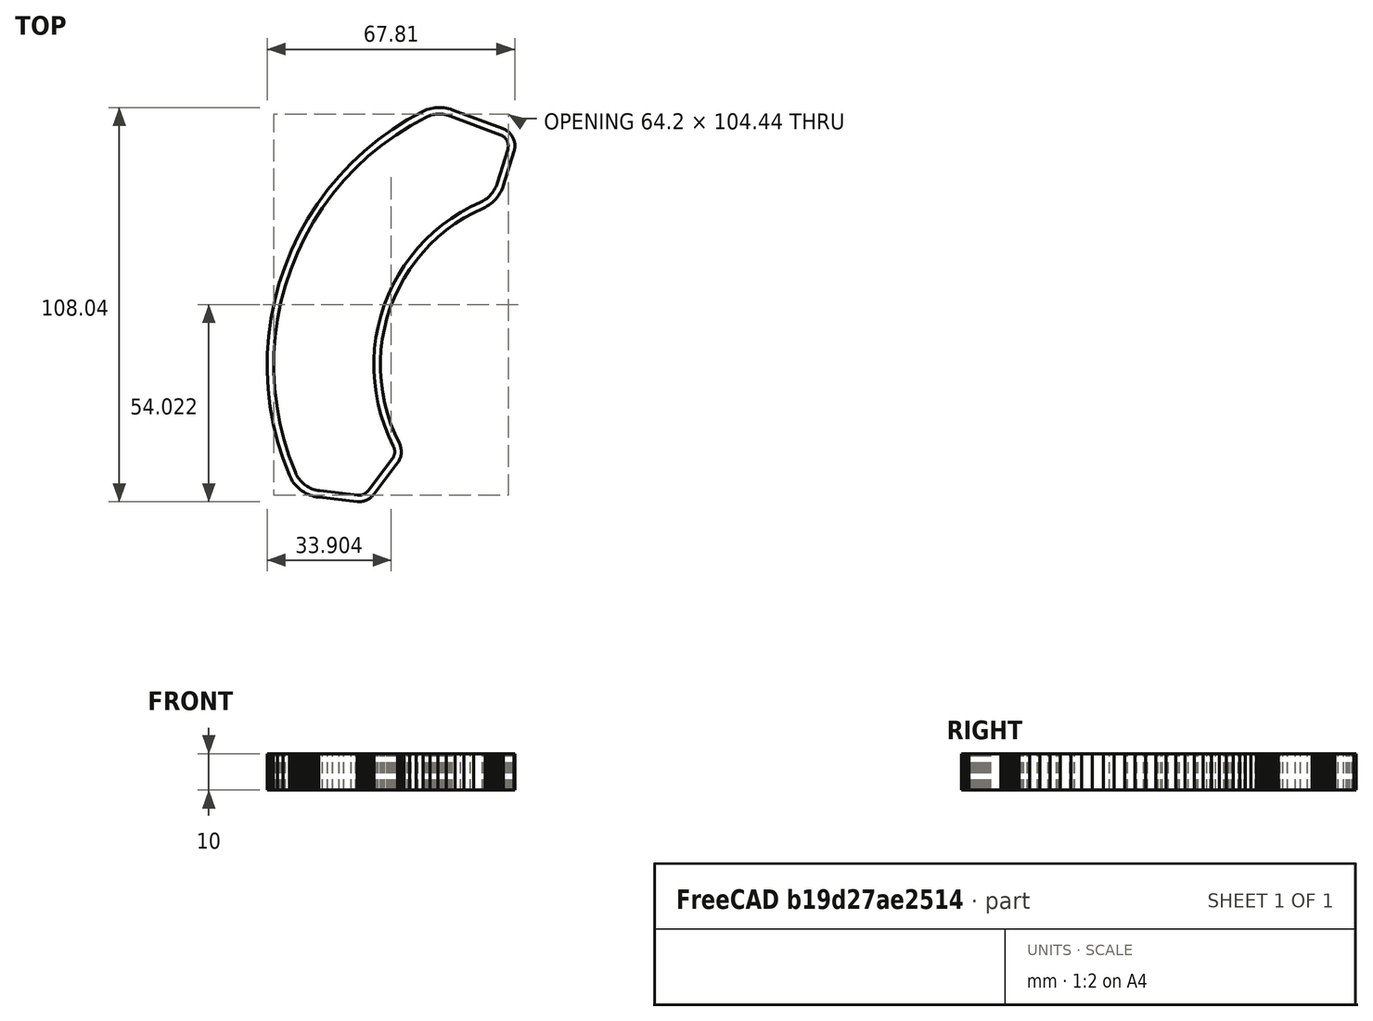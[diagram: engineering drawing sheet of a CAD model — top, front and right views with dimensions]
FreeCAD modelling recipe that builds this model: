
FCSTD DOCUMENT  (FreeCAD 1.0R39109 (Git))
Label: oledprofile
License: All rights reserved
LicenseURL: https://en.wikipedia.org/wiki/All_rights_reserved
objects: Part::Feature×1, Part::Refine×1, Part::Part2DObjectPython×1, Sketcher::SketchObject×1, PartDesign::Pad×1, PartDesign::Body×1
note: 9 computed .brp shape members not serialized (recipe doc carries the construction recipe); baked Part::Feature solids carry a one-line shape summary decoded from their .brp

FEATURE [Part::Feature] oledpart001_solid001  label="oledpart001 (Solid)001"
  shape: bbox 67.8 x 108 x 4 mm, 10964 faces (baked)
FEATURE [Part::Refine] oledpart001_solid002  label="oledpart001 (Solid)002"
  Placement = pos=(-283,298,0) rot=(0,0,1;0rad)
  Source = -> oledpart001_solid001
FEATURE [Part::Part2DObjectPython] Shape2DView  # Draft 2D object (typed FeaturePython)
  AutoUpdate = true
  Base = -> oledpart001_solid002
  Clip = false
  FuseArch = false
  HiddenLines = false
  InPlace = true
  OnlySolids = false
  Projection = (0,0,1)
  ProjectionMode = 0
  SegmentLength = 0.05
  Tessellation = false
  VisibleOnly = false
FEATURE [Sketcher::SketchObject] Sketch
  ArcFitTolerance = 1e-06
  FullyConstrained = false
  MakeInternals = false
  sketch-geometry (2716):
    g0: LineSegment StartX=4.71191 StartY=-20.0049 StartZ=0 EndX=4.70312 EndY=-17.0566 EndZ=0
    g1: LineSegment StartX=4.70312 StartY=-17.0566 StartZ=0 EndX=4.87988 EndY=-14.1143 EndZ=0
    g2: LineSegment StartX=4.87988 StartY=-14.1143 StartZ=0 EndX=5.24121 EndY=-11.1885 EndZ=0
    g3: LineSegment StartX=5.24121 StartY=-11.1885 StartZ=0 EndX=5.78613 EndY=-8.29102 EndZ=0
    g4: LineSegment StartX=5.78613 StartY=-8.29102 StartZ=0 EndX=6.51074 EndY=-5.43262 EndZ=0
    g5: LineSegment StartX=6.51074 StartY=-5.43262 StartZ=0 EndX=7.41406 EndY=-2.62695 EndZ=0
    g6: LineSegment StartX=7.41406 StartY=-2.62695 StartZ=0 EndX=8.49121 EndY=0.118164 EndZ=0
    g7: LineSegment StartX=8.49121 StartY=0.118164 StartZ=0 EndX=9.73828 EndY=2.78906 EndZ=0
    g8: LineSegment StartX=9.73828 StartY=2.78906 StartZ=0 EndX=11.1514 EndY=5.37695 EndZ=0
    g9: LineSegment StartX=11.1514 StartY=5.37695 StartZ=0 EndX=12.7236 EndY=7.87012 EndZ=0
    g10: LineSegment StartX=12.7236 StartY=7.87012 StartZ=0 EndX=14.4492 EndY=10.2607 EndZ=0
    g11: LineSegment StartX=14.4492 StartY=10.2607 StartZ=0 EndX=16.3213 EndY=12.5381 EndZ=0
    g12: LineSegment StartX=16.3213 StartY=12.5381 StartZ=0 EndX=18.332 EndY=14.6934 EndZ=0
    g13: LineSegment StartX=18.332 StartY=14.6934 StartZ=0 EndX=20.4756 EndY=16.7188 EndZ=0
    g14: LineSegment StartX=20.4756 StartY=16.7188 StartZ=0 EndX=22.7412 EndY=18.6045 EndZ=0
    g15: LineSegment StartX=22.7412 StartY=18.6045 StartZ=0 EndX=25.1201 EndY=20.3457 EndZ=0
    g16: LineSegment StartX=25.1201 StartY=20.3457 StartZ=0 EndX=27.6045 EndY=21.9326 EndZ=0
    g17: LineSegment StartX=27.6045 StartY=21.9326 StartZ=0 EndX=30.1836 EndY=23.3613 EndZ=0
    g18: LineSegment StartX=30.1836 StartY=23.3613 StartZ=0 EndX=32.8467 EndY=24.626 EndZ=0
    g19: LineSegment StartX=32.8467 StartY=24.626 StartZ=0 EndX=33.4014 EndY=24.8887 EndZ=0
    g20: LineSegment StartX=33.4014 StartY=24.8887 StartZ=0 EndX=33.9395 EndY=25.1855 EndZ=0
    g21: LineSegment StartX=33.9395 StartY=25.1855 StartZ=0 EndX=34.459 EndY=25.5146 EndZ=0
    g22: LineSegment StartX=34.459 StartY=25.5146 StartZ=0 EndX=34.9561 EndY=25.875 EndZ=0
    g23: LineSegment StartX=34.9561 StartY=25.875 StartZ=0 EndX=35.4307 EndY=26.2646 EndZ=0
    g24: LineSegment StartX=35.4307 StartY=26.2646 StartZ=0 EndX=35.8799 EndY=26.6836 EndZ=0
    g25: LineSegment StartX=35.8799 StartY=26.6836 StartZ=0 EndX=36.3037 EndY=27.1289 EndZ=0
    g26: LineSegment StartX=36.3037 StartY=27.1289 StartZ=0 EndX=36.6982 EndY=27.5996 EndZ=0
    g27: LineSegment StartX=36.6982 StartY=27.5996 StartZ=0 EndX=37.0635 EndY=28.0928 EndZ=0
    g28: LineSegment StartX=37.0635 StartY=28.0928 StartZ=0 EndX=37.3975 EndY=28.6084 EndZ=0
    g29: LineSegment StartX=37.3975 StartY=28.6084 StartZ=0 EndX=37.7002 EndY=29.1436 EndZ=0
    g30: LineSegment StartX=37.7002 StartY=29.1436 StartZ=0 EndX=37.9688 EndY=29.6963 EndZ=0
    g31: LineSegment StartX=37.9688 StartY=29.6963 StartZ=0 EndX=38.2021 EndY=30.2637 EndZ=0
    g32: LineSegment StartX=38.2021 StartY=30.2637 StartZ=0 EndX=38.4014 EndY=30.8447 EndZ=0
    g33: LineSegment StartX=38.4014 StartY=30.8447 StartZ=0 EndX=41.2842 EndY=40.2012 EndZ=0
    g34: LineSegment StartX=41.2842 StartY=40.2012 StartZ=0 EndX=41.3643 EndY=40.4922 EndZ=0
    g35: LineSegment StartX=41.3643 StartY=40.4922 StartZ=0 EndX=41.4268 EndY=40.7881 EndZ=0
    g36: LineSegment StartX=41.4268 StartY=40.7881 StartZ=0 EndX=41.4717 EndY=41.0869 EndZ=0
    g37: LineSegment StartX=41.4717 StartY=41.0869 StartZ=0 EndX=41.498 EndY=41.3877 EndZ=0
    g38: LineSegment StartX=41.498 StartY=41.3877 StartZ=0 EndX=41.5059 EndY=41.6895 EndZ=0
    g39: LineSegment StartX=41.5059 StartY=41.6895 StartZ=0 EndX=41.4961 EndY=41.9912 EndZ=0
    g40: LineSegment StartX=41.4961 StartY=41.9912 StartZ=0 EndX=41.4678 EndY=42.292 EndZ=0
    g41: LineSegment StartX=41.4678 StartY=42.292 StartZ=0 EndX=41.4209 EndY=42.5908 EndZ=0
    g42: LineSegment StartX=41.4209 StartY=42.5908 StartZ=0 EndX=41.3564 EndY=42.8857 EndZ=0
    g43: LineSegment StartX=41.3564 StartY=42.8857 StartZ=0 EndX=41.2744 EndY=43.1768 EndZ=0
    g44: LineSegment StartX=41.2744 StartY=43.1768 StartZ=0 EndX=41.1748 EndY=43.4619 EndZ=0
    g45: LineSegment StartX=41.1748 StartY=43.4619 StartZ=0 EndX=41.0586 EndY=43.7412 EndZ=0
    g46: LineSegment StartX=41.0586 StartY=43.7412 StartZ=0 EndX=40.9258 EndY=44.0127 EndZ=0
    g47: LineSegment StartX=40.9258 StartY=44.0127 StartZ=0 EndX=40.7764 EndY=44.2754 EndZ=0
    g48: LineSegment StartX=40.7764 StartY=44.2754 StartZ=0 EndX=40.6113 EndY=44.5283 EndZ=0
    g49: LineSegment StartX=40.6113 StartY=44.5283 StartZ=0 EndX=40.4307 EndY=44.7705 EndZ=0
    g50: LineSegment StartX=40.4307 StartY=44.7705 StartZ=0 EndX=40.2363 EndY=45.002 EndZ=0
    g51: LineSegment StartX=40.2363 StartY=45.002 StartZ=0 EndX=40.0293 EndY=45.2217 EndZ=0
    g52: LineSegment StartX=40.0293 StartY=45.2217 StartZ=0 EndX=39.8076 EndY=45.4277 EndZ=0
    g53: LineSegment StartX=39.8076 StartY=45.4277 StartZ=0 EndX=39.5752 EndY=45.6201 EndZ=0
    g54: LineSegment StartX=39.5752 StartY=45.6201 StartZ=0 EndX=39.3311 EndY=45.7988 EndZ=0
    g55: LineSegment StartX=39.3311 StartY=45.7988 StartZ=0 EndX=39.0771 EndY=45.9619 EndZ=0
    g56: LineSegment StartX=39.0771 StartY=45.9619 StartZ=0 EndX=38.8135 EndY=46.1094 EndZ=0
    g57: LineSegment StartX=38.8135 StartY=46.1094 StartZ=0 EndX=38.541 EndY=46.2402 EndZ=0
    g58: LineSegment StartX=38.541 StartY=46.2402 StartZ=0 EndX=38.2617 EndY=46.3555 EndZ=0
    g59: LineSegment StartX=38.2617 StartY=46.3555 StartZ=0 EndX=24.3916 EndY=51.5547 EndZ=0
    g60: LineSegment StartX=24.3916 StartY=51.5547 StartZ=0 EndX=23.8311 EndY=51.7461 EndZ=0
    g61: LineSegment StartX=23.8311 StartY=51.7461 StartZ=0 EndX=23.2607 EndY=51.9033 EndZ=0
    g62: LineSegment StartX=23.2607 StartY=51.9033 StartZ=0 EndX=22.6826 EndY=52.0273 EndZ=0
    g63: LineSegment StartX=22.6826 StartY=52.0273 StartZ=0 EndX=22.0977 EndY=52.1162 EndZ=0
    g64: LineSegment StartX=22.0977 StartY=52.1162 StartZ=0 EndX=21.5088 EndY=52.1709 EndZ=0
    g65: LineSegment StartX=21.5088 StartY=52.1709 StartZ=0 EndX=20.918 EndY=52.1904 EndZ=0
    g66: LineSegment StartX=20.918 StartY=52.1904 StartZ=0 EndX=20.3262 EndY=52.1758 EndZ=0
    g67: LineSegment StartX=20.3262 StartY=52.1758 StartZ=0 EndX=19.7363 EndY=52.125 EndZ=0
    g68: LineSegment StartX=19.7363 StartY=52.125 StartZ=0 EndX=19.1514 EndY=52.04 EndZ=0
    g69: LineSegment StartX=19.1514 StartY=52.04 StartZ=0 EndX=18.5723 EndY=51.9209 EndZ=0
    g70: LineSegment StartX=18.5723 StartY=51.9209 StartZ=0 EndX=18.001 EndY=51.7676 EndZ=0
    g71: LineSegment StartX=18.001 StartY=51.7676 StartZ=0 EndX=17.4395 EndY=51.5801 EndZ=0
    g72: LineSegment StartX=17.4395 StartY=51.5801 StartZ=0 EndX=16.8906 EndY=51.3604 EndZ=0
    g73: LineSegment StartX=16.8906 StartY=51.3604 StartZ=0 EndX=16.3555 EndY=51.1084 EndZ=0
    g74: LineSegment StartX=16.3555 StartY=51.1084 StartZ=0 EndX=12.0879 EndY=48.7725 EndZ=0
    g75: LineSegment StartX=12.0879 StartY=48.7725 StartZ=0 EndX=7.97461 EndY=46.1748 EndZ=0
    g76: LineSegment StartX=7.97461 StartY=46.1748 StartZ=0 EndX=4.03223 EndY=43.3252 EndZ=0
    g77: LineSegment StartX=4.03223 StartY=43.3252 StartZ=0 EndX=0.274414 EndY=40.2354 EndZ=0
    g78: LineSegment StartX=0.274414 StartY=40.2354 StartZ=0 EndX=-3.2832 EndY=36.918 EndZ=0
    g79: LineSegment StartX=-3.2832 StartY=36.918 StartZ=0 EndX=-6.62695 EndY=33.3848 EndZ=0
    g80: LineSegment StartX=-6.62695 StartY=33.3848 StartZ=0 EndX=-9.74414 EndY=29.6494 EndZ=0
    g81: LineSegment StartX=-9.74414 StartY=29.6494 StartZ=0 EndX=-12.6221 EndY=25.7275 EndZ=0
    g82: LineSegment StartX=-12.6221 StartY=25.7275 StartZ=0 EndX=-15.249 EndY=21.6338 EndZ=0
    g83: LineSegment StartX=-15.249 StartY=21.6338 StartZ=0 EndX=-17.6162 EndY=17.3838 EndZ=0
    g84: LineSegment StartX=-17.6162 StartY=17.3838 StartZ=0 EndX=-19.7139 EndY=12.9941 EndZ=0
    g85: LineSegment StartX=-19.7139 StartY=12.9941 StartZ=0 EndX=-21.5332 EndY=8.48242 EndZ=0
    g86: LineSegment StartX=-21.5332 StartY=8.48242 StartZ=0 EndX=-23.0674 EndY=3.86621 EndZ=0
    g87: LineSegment StartX=-23.0674 StartY=3.86621 StartZ=0 EndX=-24.3115 EndY=-0.836914 EndZ=0
    g88: LineSegment StartX=-24.3115 StartY=-0.836914 StartZ=0 EndX=-25.2588 EndY=-5.6084 EndZ=0
    g89: LineSegment StartX=-25.2588 StartY=-5.6084 StartZ=0 EndX=-25.9072 EndY=-10.4297 EndZ=0
    g90: LineSegment StartX=-25.9072 StartY=-10.4297 StartZ=0 EndX=-26.2539 EndY=-15.2822 EndZ=0
    g91: LineSegment StartX=-26.2539 StartY=-15.2822 StartZ=0 EndX=-26.2959 EndY=-20.1465 EndZ=0
    g92: LineSegment StartX=-26.2959 StartY=-20.1465 StartZ=0 EndX=-26.0361 EndY=-25.0039 EndZ=0
    g93: LineSegment StartX=-26.0361 StartY=-25.0039 StartZ=0 EndX=-25.4727 EndY=-29.8359 EndZ=0
    g94: LineSegment StartX=-25.4727 StartY=-29.8359 StartZ=0 EndX=-24.6094 EndY=-34.623 EndZ=0
    g95: LineSegment StartX=-24.6094 StartY=-34.623 StartZ=0 EndX=-23.4492 EndY=-39.3477 EndZ=0
    g96: LineSegment StartX=-23.4492 StartY=-39.3477 StartZ=0 EndX=-21.9961 EndY=-43.9902 EndZ=0
    g97: LineSegment StartX=-21.9961 StartY=-43.9902 StartZ=0 EndX=-20.2568 EndY=-48.5332 EndZ=0
    g98: LineSegment StartX=-20.2568 StartY=-48.5332 StartZ=0 EndX=-19.998 EndY=-49.1006 EndZ=0
    g99: LineSegment StartX=-19.998 StartY=-49.1006 StartZ=0 EndX=-19.7051 EndY=-49.6504 EndZ=0
    g100: LineSegment StartX=-19.7051 StartY=-49.6504 StartZ=0 EndX=-19.377 EndY=-50.1807 EndZ=0
    g101: LineSegment StartX=-19.377 StartY=-50.1807 StartZ=0 EndX=-19.0176 EndY=-50.6895 EndZ=0
    g102: LineSegment StartX=-19.0176 StartY=-50.6895 StartZ=0 EndX=-18.627 EndY=-51.1758 EndZ=0
    g103: LineSegment StartX=-18.627 StartY=-51.1758 StartZ=0 EndX=-18.207 EndY=-51.6357 EndZ=0
    g104: LineSegment StartX=-18.207 StartY=-51.6357 StartZ=0 EndX=-17.7588 EndY=-52.0693 EndZ=0
    g105: LineSegment StartX=-17.7588 StartY=-52.0693 StartZ=0 EndX=-17.2852 EndY=-52.4736 EndZ=0
    g106: LineSegment StartX=-17.2852 StartY=-52.4736 StartZ=0 EndX=-16.7861 EndY=-52.8477 EndZ=0
    g107: LineSegment StartX=-16.7861 StartY=-52.8477 StartZ=0 EndX=-16.2656 EndY=-53.1904 EndZ=0
    g108: LineSegment StartX=-16.2656 StartY=-53.1904 StartZ=0 EndX=-15.7246 EndY=-53.5 EndZ=0
    g109: LineSegment StartX=-15.7246 StartY=-53.5 StartZ=0 EndX=-15.165 EndY=-53.7754 EndZ=0
    g110: LineSegment StartX=-15.165 StartY=-53.7754 StartZ=0 EndX=-14.5898 EndY=-54.0146 EndZ=0
    g111: LineSegment StartX=-14.5898 StartY=-54.0146 StartZ=0 EndX=-14.001 EndY=-54.2178 EndZ=0
    g112: LineSegment StartX=-14.001 StartY=-54.2178 StartZ=0 EndX=-13.4004 EndY=-54.3838 EndZ=0
    g113: LineSegment StartX=-13.4004 StartY=-54.3838 StartZ=0 EndX=-12.79 EndY=-54.5127 EndZ=0
    g114: LineSegment StartX=-12.79 StartY=-54.5127 StartZ=0 EndX=-12.1738 EndY=-54.6025 EndZ=0
    g115: LineSegment StartX=-12.1738 StartY=-54.6025 StartZ=0 EndX=-1.70898 EndY=-55.8027 EndZ=0
    g116: LineSegment StartX=-1.70898 StartY=-55.8027 StartZ=0 EndX=-1.70996 EndY=-55.8145 EndZ=0
    g117: LineSegment StartX=-1.70996 StartY=-55.8145 StartZ=0 EndX=-1.4043 EndY=-55.8398 EndZ=0
    g118: LineSegment StartX=-1.4043 StartY=-55.8398 StartZ=0 EndX=-1.09766 EndY=-55.8467 EndZ=0
    g119: LineSegment StartX=-1.09766 StartY=-55.8467 StartZ=0 EndX=-0.791992 EndY=-55.835 EndZ=0
    g120: LineSegment StartX=-0.791992 StartY=-55.835 StartZ=0 EndX=-0.487305 EndY=-55.8047 EndZ=0
    g121: LineSegment StartX=-0.487305 StartY=-55.8047 StartZ=0 EndX=-0.18457 EndY=-55.7549 EndZ=0
    g122: LineSegment StartX=-0.18457 StartY=-55.7549 StartZ=0 EndX=0.114258 EndY=-55.6875 EndZ=0
    g123: LineSegment StartX=0.114258 StartY=-55.6875 StartZ=0 EndX=0.40918 EndY=-55.6016 EndZ=0
    g124: LineSegment StartX=0.40918 StartY=-55.6016 StartZ=0 EndX=0.697266 EndY=-55.4971 EndZ=0
    g125: LineSegment StartX=0.697266 StartY=-55.4971 StartZ=0 EndX=0.978516 EndY=-55.376 EndZ=0
    g126: LineSegment StartX=0.978516 StartY=-55.376 StartZ=0 EndX=1.25195 EndY=-55.2373 EndZ=0
    g127: LineSegment StartX=1.25195 StartY=-55.2373 StartZ=0 EndX=1.5166 EndY=-55.083 EndZ=0
    g128: LineSegment StartX=1.5166 StartY=-55.083 StartZ=0 EndX=1.77148 EndY=-54.9121 EndZ=0
    g129: LineSegment StartX=1.77148 StartY=-54.9121 StartZ=0 EndX=2.01465 EndY=-54.7256 EndZ=0
    g130: LineSegment StartX=2.01465 StartY=-54.7256 StartZ=0 EndX=2.24609 EndY=-54.5254 EndZ=0
    g131: LineSegment StartX=2.24609 StartY=-54.5254 StartZ=0 EndX=2.46582 EndY=-54.3105 EndZ=0
    g132: LineSegment StartX=2.46582 StartY=-54.3105 StartZ=0 EndX=2.6709 EndY=-54.084 EndZ=0
    g133: LineSegment StartX=2.6709 StartY=-54.084 StartZ=0 EndX=2.8623 EndY=-53.8438 EndZ=0
    g134: LineSegment StartX=2.8623 StartY=-53.8438 StartZ=0 EndX=9.4082 EndY=-45.1006 EndZ=0
    g135: LineSegment StartX=9.4082 StartY=-45.1006 StartZ=0 EndX=9.58594 EndY=-44.8467 EndZ=0
    g136: LineSegment StartX=9.58594 StartY=-44.8467 StartZ=0 EndX=9.74805 EndY=-44.582 EndZ=0
    g137: LineSegment StartX=9.74805 StartY=-44.582 StartZ=0 EndX=9.89355 EndY=-44.3086 EndZ=0
    g138: LineSegment StartX=9.89355 StartY=-44.3086 StartZ=0 EndX=10.0215 EndY=-44.0254 EndZ=0
    g139: LineSegment StartX=10.0215 StartY=-44.0254 StartZ=0 EndX=10.1318 EndY=-43.7363 EndZ=0
    g140: LineSegment StartX=10.1318 StartY=-43.7363 StartZ=0 EndX=10.2236 EndY=-43.4404 EndZ=0
    g141: LineSegment StartX=10.2236 StartY=-43.4404 StartZ=0 EndX=10.2979 EndY=-43.1387 EndZ=0
    g142: LineSegment StartX=10.2979 StartY=-43.1387 StartZ=0 EndX=10.3525 EndY=-42.834 EndZ=0
    g143: LineSegment StartX=10.3525 StartY=-42.834 StartZ=0 EndX=10.3877 EndY=-42.5254 EndZ=0
    g144: LineSegment StartX=10.3877 StartY=-42.5254 StartZ=0 EndX=10.4043 EndY=-42.2158 EndZ=0
    g145: LineSegment StartX=10.4043 StartY=-42.2158 StartZ=0 EndX=10.4023 EndY=-41.9062 EndZ=0
    g146: LineSegment StartX=10.4023 StartY=-41.9062 StartZ=0 EndX=10.3799 EndY=-41.5967 EndZ=0
    g147: LineSegment StartX=10.3799 StartY=-41.5967 StartZ=0 EndX=10.3389 EndY=-41.2891 EndZ=0
    g148: LineSegment StartX=10.3389 StartY=-41.2891 StartZ=0 EndX=10.2793 EndY=-40.9854 EndZ=0
    g149: LineSegment StartX=10.2793 StartY=-40.9854 StartZ=0 EndX=10.2002 EndY=-40.6855 EndZ=0
    g150: LineSegment StartX=10.2002 StartY=-40.6855 StartZ=0 EndX=10.1035 EndY=-40.3906 EndZ=0
    g151: LineSegment StartX=10.1035 StartY=-40.3906 StartZ=0 EndX=9.98828 EndY=-40.1025 EndZ=0
    g152: LineSegment StartX=9.98828 StartY=-40.1025 StartZ=0 EndX=9.85547 EndY=-39.8223 EndZ=0
    g153: LineSegment StartX=9.85547 StartY=-39.8223 StartZ=0 EndX=8.59277 EndY=-37.1582 EndZ=0
    g154: LineSegment StartX=8.59277 StartY=-37.1582 StartZ=0 EndX=7.50098 EndY=-34.4199 EndZ=0
    g155: LineSegment StartX=7.50098 StartY=-34.4199 StartZ=0 EndX=6.58301 EndY=-31.6182 EndZ=0
    g156: LineSegment StartX=6.58301 StartY=-31.6182 StartZ=0 EndX=5.8418 EndY=-28.7646 EndZ=0
    g157: LineSegment StartX=5.8418 StartY=-28.7646 StartZ=0 EndX=5.28223 EndY=-25.8701 EndZ=0
    g158: LineSegment StartX=5.28223 StartY=-25.8701 StartZ=0 EndX=4.9043 EndY=-22.9463 EndZ=0
    g159: LineSegment StartX=4.9043 StartY=-22.9463 StartZ=0 EndX=4.71191 EndY=-20.0049 EndZ=0
    g160: LineSegment StartX=3.50488 StartY=-26.1572 StartZ=0 EndX=4.08594 EndY=-29.1621 EndZ=0
    g161: LineSegment StartX=4.08594 StartY=-29.1621 StartZ=0 EndX=4.85547 EndY=-32.125 EndZ=0
    g162: LineSegment StartX=4.85547 StartY=-32.125 StartZ=0 EndX=5.80859 EndY=-35.0342 EndZ=0
    g163: LineSegment StartX=5.80859 StartY=-35.0342 StartZ=0 EndX=6.94336 EndY=-37.877 EndZ=0
    g164: LineSegment StartX=6.94336 StartY=-37.877 StartZ=0 EndX=8.25391 EndY=-40.6436 EndZ=0
    g165: LineSegment StartX=8.25391 StartY=-40.6436 StartZ=0 EndX=8.33887 EndY=-40.8232 EndZ=0
    g166: LineSegment StartX=8.33887 StartY=-40.8232 StartZ=0 EndX=8.41211 EndY=-41.0078 EndZ=0
    g167: LineSegment StartX=8.41211 StartY=-41.0078 StartZ=0 EndX=8.47461 EndY=-41.1963 EndZ=0
    g168: LineSegment StartX=8.47461 StartY=-41.1963 StartZ=0 EndX=8.52441 EndY=-41.3877 EndZ=0
    g169: LineSegment StartX=8.52441 StartY=-41.3877 StartZ=0 EndX=8.56348 EndY=-41.582 EndZ=0
    g170: LineSegment StartX=8.56348 StartY=-41.582 StartZ=0 EndX=8.58984 EndY=-41.7793 EndZ=0
    g171: LineSegment StartX=8.58984 StartY=-41.7793 StartZ=0 EndX=8.60352 EndY=-41.9775 EndZ=0
    g172: LineSegment StartX=8.60352 StartY=-41.9775 StartZ=0 EndX=8.60547 EndY=-42.1758 EndZ=0
    g173: LineSegment StartX=8.60547 StartY=-42.1758 StartZ=0 EndX=8.59473 EndY=-42.374 EndZ=0
    g174: LineSegment StartX=8.59473 StartY=-42.374 StartZ=0 EndX=8.57129 EndY=-42.5713 EndZ=0
    g175: LineSegment StartX=8.57129 StartY=-42.5713 StartZ=0 EndX=8.53613 EndY=-42.7666 EndZ=0
    g176: LineSegment StartX=8.53613 StartY=-42.7666 StartZ=0 EndX=8.48926 EndY=-42.959 EndZ=0
    g177: LineSegment StartX=8.48926 StartY=-42.959 StartZ=0 EndX=8.43066 EndY=-43.1484 EndZ=0
    g178: LineSegment StartX=8.43066 StartY=-43.1484 StartZ=0 EndX=8.36035 EndY=-43.334 EndZ=0
    g179: LineSegment StartX=8.36035 StartY=-43.334 StartZ=0 EndX=8.27832 EndY=-43.5146 EndZ=0
    g180: LineSegment StartX=8.27832 StartY=-43.5146 StartZ=0 EndX=8.18555 EndY=-43.6904 EndZ=0
    g181: LineSegment StartX=8.18555 StartY=-43.6904 StartZ=0 EndX=8.08105 EndY=-43.8594 EndZ=0
    g182: LineSegment StartX=8.08105 StartY=-43.8594 StartZ=0 EndX=7.96777 EndY=-44.0215 EndZ=0
    g183: LineSegment StartX=7.96777 StartY=-44.0215 StartZ=0 EndX=1.4209 EndY=-52.7646 EndZ=0
    g184: LineSegment StartX=1.4209 StartY=-52.7646 StartZ=0 EndX=1.29883 EndY=-52.9189 EndZ=0
    g185: LineSegment StartX=1.29883 StartY=-52.9189 StartZ=0 EndX=1.16699 EndY=-53.0645 EndZ=0
    g186: LineSegment StartX=1.16699 StartY=-53.0645 StartZ=0 EndX=1.02734 EndY=-53.2012 EndZ=0
    g187: LineSegment StartX=1.02734 StartY=-53.2012 StartZ=0 EndX=0.878906 EndY=-53.3301 EndZ=0
    g188: LineSegment StartX=0.878906 StartY=-53.3301 StartZ=0 EndX=0.722656 EndY=-53.4492 EndZ=0
    g189: LineSegment StartX=0.722656 StartY=-53.4492 StartZ=0 EndX=0.560547 EndY=-53.5576 EndZ=0
    g190: LineSegment StartX=0.560547 StartY=-53.5576 StartZ=0 EndX=0.390625 EndY=-53.6572 EndZ=0
    g191: LineSegment StartX=0.390625 StartY=-53.6572 StartZ=0 EndX=0.21582 EndY=-53.7461 EndZ=0
    g192: LineSegment StartX=0.21582 StartY=-53.7461 StartZ=0 EndX=0.0361328 EndY=-53.8232 EndZ=0
    g193: LineSegment StartX=0.0361328 StartY=-53.8232 StartZ=0 EndX=-0.148438 EndY=-53.8896 EndZ=0
    g194: LineSegment StartX=-0.148438 StartY=-53.8896 StartZ=0 EndX=-0.336914 EndY=-53.9453 EndZ=0
    g195: LineSegment StartX=-0.336914 StartY=-53.9453 StartZ=0 EndX=-0.52832 EndY=-53.9883 EndZ=0
    g196: LineSegment StartX=-0.52832 StartY=-53.9883 StartZ=0 EndX=-0.72168 EndY=-54.0195 EndZ=0
    g197: LineSegment StartX=-0.72168 StartY=-54.0195 StartZ=0 EndX=-0.916992 EndY=-54.0391 EndZ=0
    g198: LineSegment StartX=-0.916992 StartY=-54.0391 StartZ=0 EndX=-1.11328 EndY=-54.0469 EndZ=0
    g199: LineSegment StartX=-1.11328 StartY=-54.0469 StartZ=0 EndX=-1.30957 EndY=-54.043 EndZ=0
    g200: LineSegment StartX=-1.30957 StartY=-54.043 StartZ=0 EndX=-1.50488 EndY=-54.0264 EndZ=0
    g201: LineSegment StartX=-1.50488 StartY=-54.0264 StartZ=0 EndX=-1.50391 EndY=-54.0146 EndZ=0
    g202: LineSegment StartX=-1.50391 StartY=-54.0146 StartZ=0 EndX=-11.9688 EndY=-52.8145 EndZ=0
    g203: LineSegment StartX=-11.9688 StartY=-52.8145 StartZ=0 EndX=-12.4736 EndY=-52.7402 EndZ=0
    g204: LineSegment StartX=-12.4736 StartY=-52.7402 StartZ=0 EndX=-12.9746 EndY=-52.6357 EndZ=0
    g205: LineSegment StartX=-12.9746 StartY=-52.6357 StartZ=0 EndX=-13.4668 EndY=-52.499 EndZ=0
    g206: LineSegment StartX=-13.4668 StartY=-52.499 StartZ=0 EndX=-13.9502 EndY=-52.332 EndZ=0
    g207: LineSegment StartX=-13.9502 StartY=-52.332 StartZ=0 EndX=-14.4219 EndY=-52.1357 EndZ=0
    g208: LineSegment StartX=-14.4219 StartY=-52.1357 StartZ=0 EndX=-14.8799 EndY=-51.9102 EndZ=0
    g209: LineSegment StartX=-14.8799 StartY=-51.9102 StartZ=0 EndX=-15.3242 EndY=-51.6562 EndZ=0
    g210: LineSegment StartX=-15.3242 StartY=-51.6562 StartZ=0 EndX=-15.751 EndY=-51.376 EndZ=0
    g211: LineSegment StartX=-15.751 StartY=-51.376 StartZ=0 EndX=-16.1602 EndY=-51.0684 EndZ=0
    g212: LineSegment StartX=-16.1602 StartY=-51.0684 StartZ=0 EndX=-16.5488 EndY=-50.7373 EndZ=0
    g213: LineSegment StartX=-16.5488 StartY=-50.7373 StartZ=0 EndX=-16.916 EndY=-50.3818 EndZ=0
    g214: LineSegment StartX=-16.916 StartY=-50.3818 StartZ=0 EndX=-17.2607 EndY=-50.0039 EndZ=0
    g215: LineSegment StartX=-17.2607 StartY=-50.0039 StartZ=0 EndX=-17.5811 EndY=-49.6064 EndZ=0
    g216: LineSegment StartX=-17.5811 StartY=-49.6064 StartZ=0 EndX=-17.876 EndY=-49.1885 EndZ=0
    g217: LineSegment StartX=-17.876 StartY=-49.1885 StartZ=0 EndX=-18.1436 EndY=-48.7539 EndZ=0
    g218: LineSegment StartX=-18.1436 StartY=-48.7539 StartZ=0 EndX=-18.3848 EndY=-48.3027 EndZ=0
    g219: LineSegment StartX=-18.3848 StartY=-48.3027 StartZ=0 EndX=-18.5967 EndY=-47.8379 EndZ=0
    g220: LineSegment StartX=-18.5967 StartY=-47.8379 StartZ=0 EndX=-20.2959 EndY=-43.3994 EndZ=0
    g221: LineSegment StartX=-20.2959 StartY=-43.3994 StartZ=0 EndX=-21.7148 EndY=-38.8643 EndZ=0
    g222: LineSegment StartX=-21.7148 StartY=-38.8643 StartZ=0 EndX=-22.8486 EndY=-34.249 EndZ=0
    g223: LineSegment StartX=-22.8486 StartY=-34.249 StartZ=0 EndX=-23.6924 EndY=-29.5723 EndZ=0
    g224: LineSegment StartX=-23.6924 StartY=-29.5723 StartZ=0 EndX=-24.2422 EndY=-24.8516 EndZ=0
    g225: LineSegment StartX=-24.2422 StartY=-24.8516 StartZ=0 EndX=-24.4971 EndY=-20.1064 EndZ=0
    g226: LineSegment StartX=-24.4971 StartY=-20.1064 StartZ=0 EndX=-24.4551 EndY=-15.3545 EndZ=0
    g227: LineSegment StartX=-24.4551 StartY=-15.3545 StartZ=0 EndX=-24.1162 EndY=-10.6133 EndZ=0
    g228: LineSegment StartX=-24.1162 StartY=-10.6133 StartZ=0 EndX=-23.4834 EndY=-5.90332 EndZ=0
    g229: LineSegment StartX=-23.4834 StartY=-5.90332 StartZ=0 EndX=-22.5576 EndY=-1.24219 EndZ=0
    g230: LineSegment StartX=-22.5576 StartY=-1.24219 StartZ=0 EndX=-21.3428 EndY=3.35156 EndZ=0
    g231: LineSegment StartX=-21.3428 StartY=3.35156 StartZ=0 EndX=-19.8438 EndY=7.86133 EndZ=0
    g232: LineSegment StartX=-19.8438 StartY=7.86133 StartZ=0 EndX=-18.0664 EndY=12.2695 EndZ=0
    g233: LineSegment StartX=-18.0664 StartY=12.2695 StartZ=0 EndX=-16.0176 EndY=16.5566 EndZ=0
    g234: LineSegment StartX=-16.0176 StartY=16.5566 StartZ=0 EndX=-13.7051 EndY=20.709 EndZ=0
    g235: LineSegment StartX=-13.7051 StartY=20.709 StartZ=0 EndX=-11.1377 EndY=24.708 EndZ=0
    g236: LineSegment StartX=-11.1377 StartY=24.708 StartZ=0 EndX=-8.32617 EndY=28.54 EndZ=0
    g237: LineSegment StartX=-8.32617 StartY=28.54 StartZ=0 EndX=-5.28223 EndY=32.1885 EndZ=0
    g238: LineSegment StartX=-5.28223 StartY=32.1885 StartZ=0 EndX=-2.01562 EndY=35.6406 EndZ=0
    g239: LineSegment StartX=-2.01562 StartY=35.6406 StartZ=0 EndX=1.45996 EndY=38.8818 EndZ=0
    g240: LineSegment StartX=1.45996 StartY=38.8818 StartZ=0 EndX=5.13086 EndY=41.9004 EndZ=0
    g241: LineSegment StartX=5.13086 StartY=41.9004 StartZ=0 EndX=8.9834 EndY=44.6836 EndZ=0
    g242: LineSegment StartX=8.9834 StartY=44.6836 StartZ=0 EndX=13.001 EndY=47.2207 EndZ=0
    g243: LineSegment StartX=13.001 StartY=47.2207 StartZ=0 EndX=17.1699 EndY=49.5029 EndZ=0
    g244: LineSegment StartX=17.1699 StartY=49.5029 StartZ=0 EndX=17.6084 EndY=49.71 EndZ=0
    g245: LineSegment StartX=17.6084 StartY=49.71 StartZ=0 EndX=18.0586 EndY=49.8896 EndZ=0
    g246: LineSegment StartX=18.0586 StartY=49.8896 StartZ=0 EndX=18.5195 EndY=50.043 EndZ=0
    g247: LineSegment StartX=18.5195 StartY=50.043 StartZ=0 EndX=18.9873 EndY=50.1689 EndZ=0
    g248: LineSegment StartX=18.9873 StartY=50.1689 StartZ=0 EndX=19.4629 EndY=50.2676 EndZ=0
    g249: LineSegment StartX=19.4629 StartY=50.2676 StartZ=0 EndX=19.9424 EndY=50.3369 EndZ=0
    g250: LineSegment StartX=19.9424 StartY=50.3369 StartZ=0 EndX=20.4258 EndY=50.3779 EndZ=0
    g251: LineSegment StartX=20.4258 StartY=50.3779 StartZ=0 EndX=20.9111 EndY=50.3906 EndZ=0
    g252: LineSegment StartX=20.9111 StartY=50.3906 StartZ=0 EndX=21.3955 EndY=50.375 EndZ=0
    g253: LineSegment StartX=21.3955 StartY=50.375 StartZ=0 EndX=21.8789 EndY=50.3301 EndZ=0
    g254: LineSegment StartX=21.8789 StartY=50.3301 StartZ=0 EndX=22.3584 EndY=50.2568 EndZ=0
    g255: LineSegment StartX=22.3584 StartY=50.2568 StartZ=0 EndX=22.833 EndY=50.1553 EndZ=0
    g256: LineSegment StartX=22.833 StartY=50.1553 StartZ=0 EndX=23.2998 EndY=50.0264 EndZ=0
    g257: LineSegment StartX=23.2998 StartY=50.0264 StartZ=0 EndX=23.7598 EndY=49.8691 EndZ=0
    g258: LineSegment StartX=23.7598 StartY=49.8691 StartZ=0 EndX=37.6299 EndY=44.6699 EndZ=0
    g259: LineSegment StartX=37.6299 StartY=44.6699 StartZ=0 EndX=37.8086 EndY=44.5967 EndZ=0
    g260: LineSegment StartX=37.8086 StartY=44.5967 StartZ=0 EndX=37.9824 EndY=44.5127 EndZ=0
    g261: LineSegment StartX=37.9824 StartY=44.5127 StartZ=0 EndX=38.1514 EndY=44.418 EndZ=0
    g262: LineSegment StartX=38.1514 StartY=44.418 StartZ=0 EndX=38.3145 EndY=44.3135 EndZ=0
    g263: LineSegment StartX=38.3145 StartY=44.3135 StartZ=0 EndX=38.4707 EndY=44.1992 EndZ=0
    g264: LineSegment StartX=38.4707 StartY=44.1992 StartZ=0 EndX=38.6191 EndY=44.0762 EndZ=0
    g265: LineSegment StartX=38.6191 StartY=44.0762 StartZ=0 EndX=38.7607 EndY=43.9443 EndZ=0
    g266: LineSegment StartX=38.7607 StartY=43.9443 StartZ=0 EndX=38.8936 EndY=43.8037 EndZ=0
    g267: LineSegment StartX=38.8936 StartY=43.8037 StartZ=0 EndX=39.0186 EndY=43.6553 EndZ=0
    g268: LineSegment StartX=39.0186 StartY=43.6553 StartZ=0 EndX=39.1328 EndY=43.5 EndZ=0
    g269: LineSegment StartX=39.1328 StartY=43.5 StartZ=0 EndX=39.2393 EndY=43.3379 EndZ=0
    g270: LineSegment StartX=39.2393 StartY=43.3379 StartZ=0 EndX=39.334 EndY=43.1699 EndZ=0
    g271: LineSegment StartX=39.334 StartY=43.1699 StartZ=0 EndX=39.4199 EndY=42.9971 EndZ=0
    g272: LineSegment StartX=39.4199 StartY=42.9971 StartZ=0 EndX=39.4941 EndY=42.8184 EndZ=0
    g273: LineSegment StartX=39.4941 StartY=42.8184 StartZ=0 EndX=39.5576 EndY=42.6357 EndZ=0
    g274: LineSegment StartX=39.5576 StartY=42.6357 StartZ=0 EndX=39.6104 EndY=42.4492 EndZ=0
    g275: LineSegment StartX=39.6104 StartY=42.4492 StartZ=0 EndX=39.6514 EndY=42.2607 EndZ=0
    g276: LineSegment StartX=39.6514 StartY=42.2607 StartZ=0 EndX=39.6816 EndY=42.0693 EndZ=0
    g277: LineSegment StartX=39.6816 StartY=42.0693 StartZ=0 EndX=39.6992 EndY=41.877 EndZ=0
    g278: LineSegment StartX=39.6992 StartY=41.877 StartZ=0 EndX=39.7061 EndY=41.6836 EndZ=0
    g279: LineSegment StartX=39.7061 StartY=41.6836 StartZ=0 EndX=39.7012 EndY=41.4902 EndZ=0
    g280: LineSegment StartX=39.7012 StartY=41.4902 StartZ=0 EndX=39.6846 EndY=41.2979 EndZ=0
    g281: LineSegment StartX=39.6846 StartY=41.2979 StartZ=0 EndX=39.6553 EndY=41.1064 EndZ=0
    g282: LineSegment StartX=39.6553 StartY=41.1064 StartZ=0 EndX=39.6152 EndY=40.917 EndZ=0
    g283: LineSegment StartX=39.6152 StartY=40.917 StartZ=0 EndX=39.5645 EndY=40.7305 EndZ=0
    g284: LineSegment StartX=39.5645 StartY=40.7305 StartZ=0 EndX=36.6816 EndY=31.375 EndZ=0
    g285: LineSegment StartX=36.6816 StartY=31.375 StartZ=0 EndX=36.5186 EndY=30.8984 EndZ=0
    g286: LineSegment StartX=36.5186 StartY=30.8984 StartZ=0 EndX=36.3262 EndY=30.4326 EndZ=0
    g287: LineSegment StartX=36.3262 StartY=30.4326 StartZ=0 EndX=36.1064 EndY=29.9795 EndZ=0
    g288: LineSegment StartX=36.1064 StartY=29.9795 StartZ=0 EndX=35.8584 EndY=29.541 EndZ=0
    g289: LineSegment StartX=35.8584 StartY=29.541 StartZ=0 EndX=35.584 EndY=29.1182 EndZ=0
    g290: LineSegment StartX=35.584 StartY=29.1182 StartZ=0 EndX=35.2842 EndY=28.7139 EndZ=0
    g291: LineSegment StartX=35.2842 StartY=28.7139 StartZ=0 EndX=34.9609 EndY=28.3281 EndZ=0
    g292: LineSegment StartX=34.9609 StartY=28.3281 StartZ=0 EndX=34.6143 EndY=27.9629 EndZ=0
    g293: LineSegment StartX=34.6143 StartY=27.9629 StartZ=0 EndX=34.2451 EndY=27.6191 EndZ=0
    g294: LineSegment StartX=34.2451 StartY=27.6191 StartZ=0 EndX=33.8564 EndY=27.2998 EndZ=0
    g295: LineSegment StartX=33.8564 StartY=27.2998 StartZ=0 EndX=33.4482 EndY=27.0039 EndZ=0
    g296: LineSegment StartX=33.4482 StartY=27.0039 StartZ=0 EndX=33.0225 EndY=26.7344 EndZ=0
    g297: LineSegment StartX=33.0225 StartY=26.7344 StartZ=0 EndX=32.582 EndY=26.4912 EndZ=0
    g298: LineSegment StartX=32.582 StartY=26.4912 StartZ=0 EndX=32.126 EndY=26.2754 EndZ=0
    g299: LineSegment StartX=32.126 StartY=26.2754 StartZ=0 EndX=29.3604 EndY=24.9629 EndZ=0
    g300: LineSegment StartX=29.3604 StartY=24.9629 StartZ=0 EndX=26.6836 EndY=23.4795 EndZ=0
    g301: LineSegment StartX=26.6836 StartY=23.4795 StartZ=0 EndX=24.1035 EndY=21.8311 EndZ=0
    g302: LineSegment StartX=24.1035 StartY=21.8311 StartZ=0 EndX=21.6328 EndY=20.0234 EndZ=0
    g303: LineSegment StartX=21.6328 StartY=20.0234 StartZ=0 EndX=19.2803 EndY=18.0645 EndZ=0
    g304: LineSegment StartX=19.2803 StartY=18.0645 StartZ=0 EndX=17.0557 EndY=15.9629 EndZ=0
    g305: LineSegment StartX=17.0557 StartY=15.9629 StartZ=0 EndX=14.9668 EndY=13.7246 EndZ=0
    g306: LineSegment StartX=14.9668 StartY=13.7246 StartZ=0 EndX=13.0234 EndY=11.3594 EndZ=0
    g307: LineSegment StartX=13.0234 StartY=11.3594 StartZ=0 EndX=11.2314 EndY=8.87793 EndZ=0
    g308: LineSegment StartX=11.2314 StartY=8.87793 StartZ=0 EndX=9.59863 EndY=6.28809 EndZ=0
    g309: LineSegment StartX=9.59863 StartY=6.28809 StartZ=0 EndX=8.13184 EndY=3.60156 EndZ=0
    g310: LineSegment StartX=8.13184 StartY=3.60156 StartZ=0 EndX=6.83691 EndY=0.828125 EndZ=0
    g311: LineSegment StartX=6.83691 StartY=0.828125 StartZ=0 EndX=5.71875 EndY=-2.02148 EndZ=0
    g312: LineSegment StartX=5.71875 StartY=-2.02148 StartZ=0 EndX=4.78125 EndY=-4.93555 EndZ=0
    g313: LineSegment StartX=4.78125 StartY=-4.93555 StartZ=0 EndX=4.02832 EndY=-7.90332 EndZ=0
    g314: LineSegment StartX=4.02832 StartY=-7.90332 StartZ=0 EndX=3.46289 EndY=-10.9111 EndZ=0
    g315: LineSegment StartX=3.46289 StartY=-10.9111 StartZ=0 EndX=3.08789 EndY=-13.9492 EndZ=0
    g316: LineSegment StartX=3.08789 StartY=-13.9492 StartZ=0 EndX=2.9043 EndY=-17.0049 EndZ=0
    g317: LineSegment StartX=2.9043 StartY=-17.0049 StartZ=0 EndX=2.91211 EndY=-20.0664 EndZ=0
    g318: LineSegment StartX=2.91211 StartY=-20.0664 StartZ=0 EndX=3.11328 EndY=-23.1211 EndZ=0
    g319: LineSegment StartX=3.11328 StartY=-23.1211 StartZ=0 EndX=3.50488 EndY=-26.1572 EndZ=0
    g320: LineSegment StartX=35.4111 StartY=40.5068 StartZ=0 EndX=35.3398 EndY=40.5781 EndZ=0
    g321: LineSegment StartX=35.3398 StartY=40.5781 StartZ=0 EndX=35.2734 EndY=40.6533 EndZ=0
    g322: LineSegment StartX=35.2734 StartY=40.6533 StartZ=0 EndX=35.2119 EndY=40.7324 EndZ=0
    g323: LineSegment StartX=35.2119 StartY=40.7324 StartZ=0 EndX=35.1553 EndY=40.8154 EndZ=0
    g324: LineSegment StartX=35.1553 StartY=40.8154 StartZ=0 EndX=35.1045 EndY=40.9023 EndZ=0
    g325: LineSegment StartX=35.1045 StartY=40.9023 StartZ=0 EndX=35.0586 EndY=40.9922 EndZ=0
    g326: LineSegment StartX=35.0586 StartY=40.9922 StartZ=0 EndX=35.0186 EndY=41.084 EndZ=0
    g327: LineSegment StartX=35.0186 StartY=41.084 StartZ=0 EndX=34.9844 EndY=41.1787 EndZ=0
    g328: LineSegment StartX=34.9844 StartY=41.1787 StartZ=0 EndX=34.9561 EndY=41.2754 EndZ=0
    g329: LineSegment StartX=34.9561 StartY=41.2754 StartZ=0 EndX=34.9346 EndY=41.373 EndZ=0
    g330: LineSegment StartX=34.9346 StartY=41.373 StartZ=0 EndX=34.9189 EndY=41.4727 EndZ=0
    g331: LineSegment StartX=34.9189 StartY=41.4727 StartZ=0 EndX=34.9092 EndY=41.5723 EndZ=0
    g332: LineSegment StartX=34.9092 StartY=41.5723 StartZ=0 EndX=34.9062 EndY=41.6729 EndZ=0
    g333: LineSegment StartX=34.9062 StartY=41.6729 StartZ=0 EndX=34.9092 EndY=41.7734 EndZ=0
    g334: LineSegment StartX=34.9092 StartY=41.7734 StartZ=0 EndX=34.9189 EndY=41.874 EndZ=0
    g335: LineSegment StartX=34.9189 StartY=41.874 StartZ=0 EndX=34.9346 EndY=41.9727 EndZ=0
    g336: LineSegment StartX=34.9346 StartY=41.9727 StartZ=0 EndX=34.9561 EndY=42.0713 EndZ=0
    g337: LineSegment StartX=34.9561 StartY=42.0713 StartZ=0 EndX=34.9844 EndY=42.168 EndZ=0
    g338: LineSegment StartX=34.9844 StartY=42.168 StartZ=0 EndX=35.0186 EndY=42.2617 EndZ=0
    g339: LineSegment StartX=35.0186 StartY=42.2617 StartZ=0 EndX=35.0586 EndY=42.3545 EndZ=0
    g340: LineSegment StartX=35.0586 StartY=42.3545 StartZ=0 EndX=35.1045 EndY=42.4443 EndZ=0
    g341: LineSegment StartX=35.1045 StartY=42.4443 StartZ=0 EndX=35.1553 EndY=42.5303 EndZ=0
    g342: LineSegment StartX=35.1553 StartY=42.5303 StartZ=0 EndX=35.2119 EndY=42.6133 EndZ=0
    g343: LineSegment StartX=35.2119 StartY=42.6133 StartZ=0 EndX=35.2734 EndY=42.6934 EndZ=0
    g344: LineSegment StartX=35.2734 StartY=42.6934 StartZ=0 EndX=35.3398 EndY=42.7686 EndZ=0
    g345: LineSegment StartX=35.3398 StartY=42.7686 StartZ=0 EndX=35.4111 EndY=42.8398 EndZ=0
    g346: LineSegment StartX=35.4111 StartY=42.8398 StartZ=0 EndX=35.4863 EndY=42.9062 EndZ=0
    g347: LineSegment StartX=35.4863 StartY=42.9062 StartZ=0 EndX=35.5654 EndY=42.9678 EndZ=0
    g348: LineSegment StartX=35.5654 StartY=42.9678 StartZ=0 EndX=35.6484 EndY=43.0244 EndZ=0
    g349: LineSegment StartX=35.6484 StartY=43.0244 StartZ=0 EndX=35.7354 EndY=43.0752 EndZ=0
    g350: LineSegment StartX=35.7354 StartY=43.0752 StartZ=0 EndX=35.8252 EndY=43.1211 EndZ=0
    g351: LineSegment StartX=35.8252 StartY=43.1211 StartZ=0 EndX=35.917 EndY=43.1611 EndZ=0
    g352: LineSegment StartX=35.917 StartY=43.1611 StartZ=0 EndX=36.0117 EndY=43.1953 EndZ=0
    g353: LineSegment StartX=36.0117 StartY=43.1953 StartZ=0 EndX=36.1084 EndY=43.2227 EndZ=0
    g354: LineSegment StartX=36.1084 StartY=43.2227 StartZ=0 EndX=36.2061 EndY=43.2451 EndZ=0
    g355: LineSegment StartX=36.2061 StartY=43.2451 StartZ=0 EndX=36.3057 EndY=43.2607 EndZ=0
    g356: LineSegment StartX=36.3057 StartY=43.2607 StartZ=0 EndX=36.4053 EndY=43.2695 EndZ=0
    g357: LineSegment StartX=36.4053 StartY=43.2695 StartZ=0 EndX=36.5059 EndY=43.2734 EndZ=0
    g358: LineSegment StartX=36.5059 StartY=43.2734 StartZ=0 EndX=36.6064 EndY=43.2695 EndZ=0
    g359: LineSegment StartX=36.6064 StartY=43.2695 StartZ=0 EndX=36.707 EndY=43.2607 EndZ=0
    g360: LineSegment StartX=36.707 StartY=43.2607 StartZ=0 EndX=36.8057 EndY=43.2451 EndZ=0
    g361: LineSegment StartX=36.8057 StartY=43.2451 StartZ=0 EndX=36.9043 EndY=43.2227 EndZ=0
    g362: LineSegment StartX=36.9043 StartY=43.2227 StartZ=0 EndX=37.001 EndY=43.1953 EndZ=0
    g363: LineSegment StartX=37.001 StartY=43.1953 StartZ=0 EndX=37.0947 EndY=43.1611 EndZ=0
    g364: LineSegment StartX=37.0947 StartY=43.1611 StartZ=0 EndX=37.1875 EndY=43.1211 EndZ=0
    g365: LineSegment StartX=37.1875 StartY=43.1211 StartZ=0 EndX=37.2773 EndY=43.0752 EndZ=0
    g366: LineSegment StartX=37.2773 StartY=43.0752 StartZ=0 EndX=37.3633 EndY=43.0244 EndZ=0
    g367: LineSegment StartX=37.3633 StartY=43.0244 StartZ=0 EndX=37.4463 EndY=42.9678 EndZ=0
    g368: LineSegment StartX=37.4463 StartY=42.9678 StartZ=0 EndX=37.5264 EndY=42.9062 EndZ=0
    g369: LineSegment StartX=37.5264 StartY=42.9062 StartZ=0 EndX=37.6016 EndY=42.8398 EndZ=0
    g370: LineSegment StartX=37.6016 StartY=42.8398 StartZ=0 EndX=37.6729 EndY=42.7686 EndZ=0
    g371: LineSegment StartX=37.6729 StartY=42.7686 StartZ=0 EndX=37.7393 EndY=42.6934 EndZ=0
    g372: LineSegment StartX=37.7393 StartY=42.6934 StartZ=0 EndX=37.8008 EndY=42.6133 EndZ=0
    g373: LineSegment StartX=37.8008 StartY=42.6133 StartZ=0 EndX=37.8574 EndY=42.5303 EndZ=0
    g374: LineSegment StartX=37.8574 StartY=42.5303 StartZ=0 EndX=37.9082 EndY=42.4443 EndZ=0
    g375: LineSegment StartX=37.9082 StartY=42.4443 StartZ=0 EndX=37.9541 EndY=42.3545 EndZ=0
    g376: LineSegment StartX=37.9541 StartY=42.3545 StartZ=0 EndX=37.9941 EndY=42.2617 EndZ=0
    g377: LineSegment StartX=37.9941 StartY=42.2617 StartZ=0 EndX=38.0283 EndY=42.168 EndZ=0
    g378: LineSegment StartX=38.0283 StartY=42.168 StartZ=0 EndX=38.0557 EndY=42.0713 EndZ=0
    g379: LineSegment StartX=38.0557 StartY=42.0713 StartZ=0 EndX=38.0781 EndY=41.9727 EndZ=0
    g380: LineSegment StartX=38.0781 StartY=41.9727 StartZ=0 EndX=38.0938 EndY=41.874 EndZ=0
    g381: LineSegment StartX=38.0938 StartY=41.874 StartZ=0 EndX=38.1035 EndY=41.7734 EndZ=0
    g382: LineSegment StartX=38.1035 StartY=41.7734 StartZ=0 EndX=38.1064 EndY=41.6729 EndZ=0
    g383: LineSegment StartX=38.1064 StartY=41.6729 StartZ=0 EndX=38.1035 EndY=41.5723 EndZ=0
    g384: LineSegment StartX=38.1035 StartY=41.5723 StartZ=0 EndX=38.0938 EndY=41.4727 EndZ=0
    g385: LineSegment StartX=38.0938 StartY=41.4727 StartZ=0 EndX=38.0781 EndY=41.373 EndZ=0
    g386: LineSegment StartX=38.0781 StartY=41.373 StartZ=0 EndX=38.0557 EndY=41.2754 EndZ=0
    g387: LineSegment StartX=38.0557 StartY=41.2754 StartZ=0 EndX=38.0283 EndY=41.1787 EndZ=0
    g388: LineSegment StartX=38.0283 StartY=41.1787 StartZ=0 EndX=37.9941 EndY=41.084 EndZ=0
    g389: LineSegment StartX=37.9941 StartY=41.084 StartZ=0 EndX=37.9541 EndY=40.9922 EndZ=0
    g390: LineSegment StartX=37.9541 StartY=40.9922 StartZ=0 EndX=37.9082 EndY=40.9023 EndZ=0
    g391: LineSegment StartX=37.9082 StartY=40.9023 StartZ=0 EndX=37.8574 EndY=40.8154 EndZ=0
    g392: LineSegment StartX=37.8574 StartY=40.8154 StartZ=0 EndX=37.8008 EndY=40.7324 EndZ=0
    g393: LineSegment StartX=37.8008 StartY=40.7324 StartZ=0 EndX=37.7393 EndY=40.6533 EndZ=0
    g394: LineSegment StartX=37.7393 StartY=40.6533 StartZ=0 EndX=37.6729 EndY=40.5781 EndZ=0
    g395: LineSegment StartX=37.6729 StartY=40.5781 StartZ=0 EndX=37.6016 EndY=40.5068 EndZ=0
    g396: LineSegment StartX=37.6016 StartY=40.5068 StartZ=0 EndX=37.5264 EndY=40.4404 EndZ=0
    g397: LineSegment StartX=37.5264 StartY=40.4404 StartZ=0 EndX=37.4463 EndY=40.3789 EndZ=0
    g398: LineSegment StartX=37.4463 StartY=40.3789 StartZ=0 EndX=37.3633 EndY=40.3223 EndZ=0
    g399: LineSegment StartX=37.3633 StartY=40.3223 StartZ=0 EndX=37.2773 EndY=40.2715 EndZ=0
    ... +2316 more geometry lines
FEATURE [PartDesign::Pad] Pad
  Direction = (0,0,1)
  Length = 10
  Length2 = 10
  Profile = -> Sketch
  ReferenceAxis = -> Sketch [N_Axis]
  Refine = true
  Suppressed = false
  Type = 0
FEATURE [PartDesign::Body] Body
  AllowCompound = false
  Group = -> [Sketch,Pad]
  Origin = -> Origin
  Tip = -> Pad
